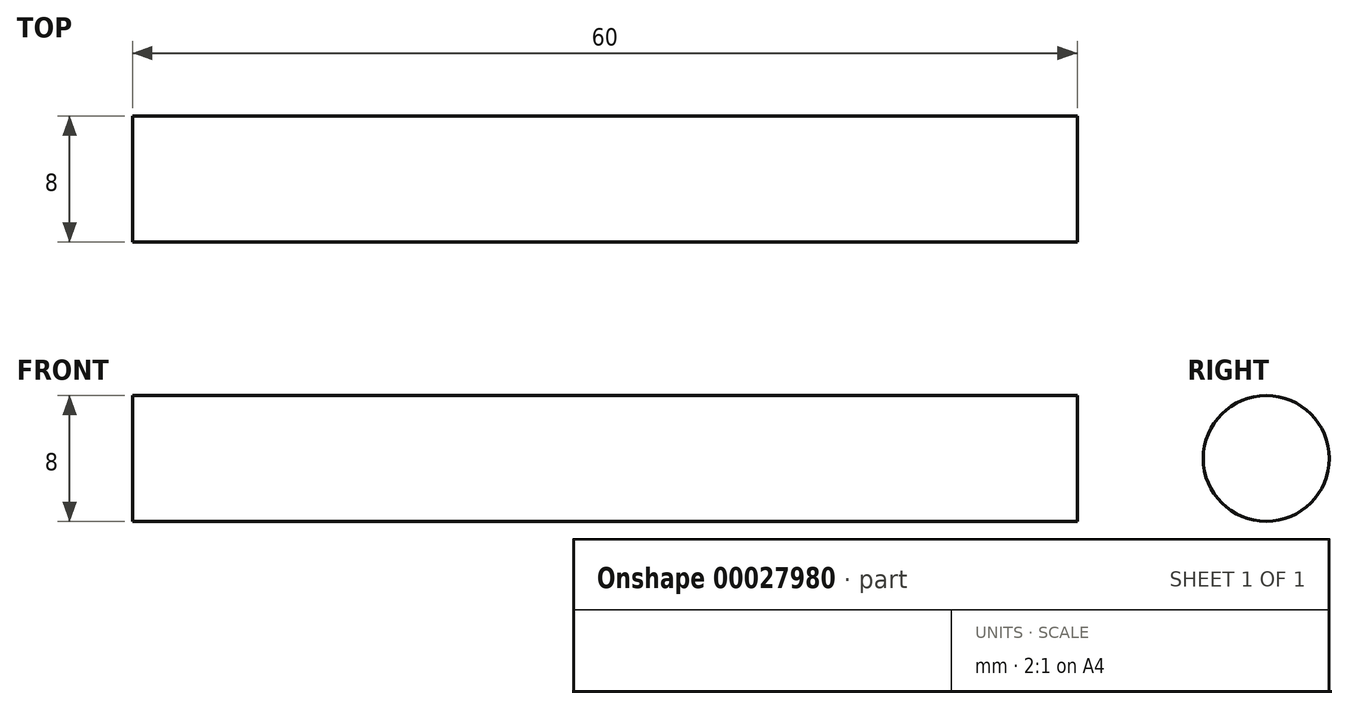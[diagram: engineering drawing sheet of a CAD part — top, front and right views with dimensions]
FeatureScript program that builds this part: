
annotation { "Feature Type Name" : "Feature", "Feature Type Description" : "" }
export const myFeature = defineFeature(function(context is Context, id is Id, definition is map)
    precondition{}
    {
        {
            var Q0;
            Q0=qCreatedBy(makeId("Right.planeOp"),FACE);
            var sketch = newSketch(context, id + "F0", { "sketchPlane" : qUnion([Q0])});
            skCircle(sketch, "E0", {"center": v(0, 0) * mm, "radius": 4 * mm});
            skSolve(sketch);
        }
        {
            var Q0;
            Q0=qSketchRegion(id+"F0",true);
            extrude(context, id + "F1", {"entities" : qUnion([Q0]), "endBound" : BoundingType.SYMMETRIC, "depth" : 60 * mm});
        }
    });
